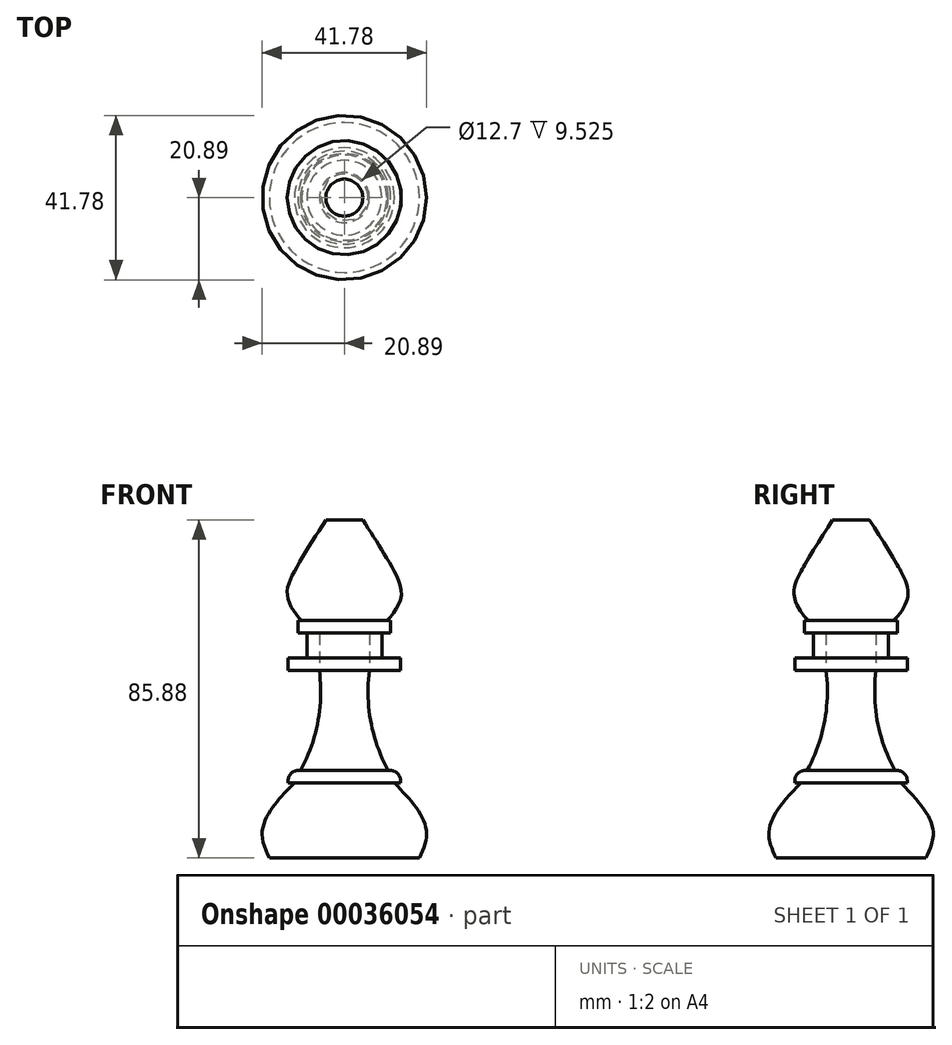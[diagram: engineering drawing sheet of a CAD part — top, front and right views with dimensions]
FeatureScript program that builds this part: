
annotation { "Feature Type Name" : "Feature", "Feature Type Description" : "" }
export const myFeature = defineFeature(function(context is Context, id is Id, definition is map)
    precondition{}
    {
        {
            var Q0;
            Q0=qCreatedBy(makeId("Top.planeOp"),FACE);
            var sketch = newSketch(context, id + "F0", { "sketchPlane" : qUnion([Q0])});
            skCircle(sketch, "E0", {"center": v(0, 0) * mm, "radius": 19.05 * mm});
            skSolve(sketch);
        }
        {
            var Q0;
            Q0=qCreatedBy(makeId("Top.planeOp"),FACE);
            cPlane(context, id + "F1", {"entities" : qUnion([Q0]), "cplaneType" : CPlaneType.OFFSET, "offset" : 19.05 * mm, "width" : 152.4 * mm, "height" : 152.4 * mm});
        }
        {
            var Q0;
            Q0=qCreatedBy(id+"F1.planeOp",FACE);
            var sketch = newSketch(context, id + "F2", { "sketchPlane" : qUnion([Q0])});
            skCircle(sketch, "E1", {"center": v(0, 0) * mm, "radius": 12.7 * mm});
            skSolve(sketch);
        }
        {
            var Q0;
            Q0=qCreatedBy(makeId("Top.planeOp"),FACE);
            cPlane(context, id + "F3", {"entities" : qUnion([Q0]), "cplaneType" : CPlaneType.OFFSET, "offset" : 5.08 * mm, "width" : 152.4 * mm, "height" : 152.4 * mm});
        }
        {
            var Q0;
            Q0=qCreatedBy(id+"F3.planeOp",FACE);
            var sketch = newSketch(context, id + "F4", { "sketchPlane" : qUnion([Q0])});
            skCircle(sketch, "E2", {"center": v(0, 0) * mm, "radius": 20.82 * mm});
            skSolve(sketch);
        }
        {
            var Q0;
            Q0=makeQuery(id+"F2.imprint","IMPRINT",FACE,{"disambiguationData":[TD([[makeQuery(id+"F2.imprint","IMPRINT",EDGE,{"derivedFrom":sQuery(id+"F2.wireOp",EDGE,"E1")}),1.0]])]});
            var Q1;
            Q1=makeQuery(id+"F4.imprint","IMPRINT",FACE,{"disambiguationData":[TD([[makeQuery(id+"F4.imprint","IMPRINT",EDGE,{"derivedFrom":sQuery(id+"F4.wireOp",EDGE,"E2")}),1.0]])]});
            var Q2;
            Q2=makeQuery(id+"F0.imprint","IMPRINT",FACE,{"disambiguationData":[TD([[makeQuery(id+"F0.imprint","IMPRINT",EDGE,{"derivedFrom":sQuery(id+"F0.wireOp",EDGE,"E0")}),1.0]])]});
            loft(context, id + "F5", {"sheetProfilesArray" : [{ "sheetProfileEntities" : qUnion([Q0]) }, { "sheetProfileEntities" : qUnion([Q1]) }, { "sheetProfileEntities" : qUnion([Q2]) }]});
        }
        {
            var Q0;
            Q0=qCreatedBy(id+"F1.planeOp",FACE);
            var sketch = newSketch(context, id + "F6", { "sketchPlane" : qUnion([Q0])});
            skCircle(sketch, "E3", {"center": v(0, 0) * mm, "radius": 14.29 * mm});
            skSolve(sketch);
        }
        {
            var Q0;
            Q0=makeQuery(id+"F6.imprint","IMPRINT",FACE,{"disambiguationData":[TD([[makeQuery(id+"F6.imprint","IMPRINT",EDGE,{"derivedFrom":sQuery(id+"F6.wireOp",EDGE,"E3")}),1.0]])]});
            var Q1;
            Q1=sQuery(id+"F6.wireOp",EDGE,"E3");
            extrude(context, id + "F7", {"entities" : qUnion([Q0]), "operationType" : NewBodyOperationType.ADD, "surfaceEntities" : qUnion([Q1]), "depth" : 3.17 * mm});
        }
        {
            var Q0;
            Q0=makeQuery(id+"F7.opExtrude","CAP_EDGE",EDGE,{"disambiguationData":[OSD([sQuery(id+"F6.wireOp",EDGE,"E3")])],"isStart":false});
            fillet(context, id + "F8", {"entities" : qUnion([Q0]), "radius" : 2.54 * mm, "tangentPropagation" : true, "allowEdgeOverflow" : false});
        }
        {
            var Q0;
            Q0=makeQuery(id+"F7.opExtrude","CAP_FACE",FACE,{"disambiguationData":[OSD([sQuery(id+"F6.wireOp",EDGE,"E3")])],"isStart":false});
            cPlane(context, id + "F9", {"entities" : qUnion([Q0]), "cplaneType" : CPlaneType.OFFSET, "offset" : 25.4 * mm, "width" : 152.4 * mm, "height" : 152.4 * mm});
        }
        {
            var Q0;
            Q0=qCreatedBy(id+"F9.planeOp",FACE);
            var sketch = newSketch(context, id + "F10", { "sketchPlane" : qUnion([Q0])});
            skCircle(sketch, "E4", {"center": v(0, 0) * mm, "radius": 6.35 * mm});
            skSolve(sketch);
        }
        {
            var Q0;
            Q0=qCreatedBy(makeId("Front.planeOp"),FACE);
            var sketch = newSketch(context, id + "F11", { "sketchPlane" : qUnion([Q0])});
            skLineSegment(sketch, "E5", {"start": v(0, 47.62) * mm, "end": v(0, 22.22) * mm});
            skLineSegment(sketch, "E6", {"start": v(0, 47.62) * mm, "end": v(6.35, 47.62) * mm});
            skArc(sketch, "E7", {"start": v(6.35, 47.62) * mm, "mid": v(6.74, 34.54) * mm, "end": v(11.16, 22.23) * mm});
            skLineSegment(sketch, "E8", {"start": v(11.16, 22.23) * mm, "end": v(0, 22.22) * mm});
            skSolve(sketch);
        }
        {
            var Q0;
            Q0=makeQuery(id+"F11.imprint","IMPRINT",FACE,{"disambiguationData":[TD([[makeQuery(id+"F11.imprint","IMPRINT",EDGE,{"derivedFrom":sQuery(id+"F11.wireOp",EDGE,"E5")}),1.0]])]});
            var Q1;
            Q1=sQuery(id+"F11.wireOp",EDGE,"E5");
            revolve(context, id + "F12", {"operationType" : NewBodyOperationType.ADD, "entities" : qUnion([Q0]), "axis" : qUnion([Q1]), "revolveType" : RevolveType.FULL});
        }
        {
            var Q0;
            Q0=makeQuery(id+"F10.imprint","IMPRINT",FACE,{"disambiguationData":[TD([[makeQuery(id+"F10.imprint","IMPRINT",EDGE,{"derivedFrom":sQuery(id+"F10.wireOp",EDGE,"E4")}),1.0]])]});
            var sketch = newSketch(context, id + "F13", { "sketchPlane" : qUnion([Q0])});
            skCircle(sketch, "E9", {"center": v(0, 0) * mm, "radius": 14.29 * mm});
            skSolve(sketch);
        }
        {
            var Q0;
            Q0=makeQuery(id+"F13.imprint","IMPRINT",FACE,{"disambiguationData":[TD([[makeQuery(id+"F13.imprint","IMPRINT",EDGE,{"derivedFrom":sQuery(id+"F13.wireOp",EDGE,"E9")}),1.0]])]});
            var Q1;
            Q1=sQuery(id+"F13.wireOp",EDGE,"E9");
            extrude(context, id + "F14", {"entities" : qUnion([Q0]), "surfaceEntities" : qUnion([Q1]), "depth" : 3.17 * mm});
        }
        {
            var Q0;
            Q0=makeQuery(id+"F14.opExtrude","CAP_FACE",FACE,{"disambiguationData":[OSD([sQuery(id+"F10.wireOp",EDGE,"E4"),sQuery(id+"F13.wireOp",EDGE,"E9")])],"isStart":false});
            var sketch = newSketch(context, id + "F15", { "sketchPlane" : qUnion([Q0])});
            skCircle(sketch, "E10", {"center": v(0, 0) * mm, "radius": 9.53 * mm});
            skSolve(sketch);
        }
        {
            var Q0;
            Q0=makeQuery(id+"F15.imprint","IMPRINT",FACE,{"disambiguationData":[TD([[makeQuery(id+"F15.imprint","IMPRINT",EDGE,{"derivedFrom":sQuery(id+"F15.wireOp",EDGE,"E10")}),1.0]])]});
            var Q1;
            Q1=sQuery(id+"F15.wireOp",EDGE,"E10");
            extrude(context, id + "F16", {"entities" : qUnion([Q0]), "operationType" : NewBodyOperationType.ADD, "surfaceEntities" : qUnion([Q1]), "depth" : 6.35 * mm});
        }
        {
            var Q0;
            Q0=makeQuery(id+"F16.opExtrude","CAP_FACE",FACE,{"disambiguationData":[OSD([sQuery(id+"F10.wireOp",EDGE,"E4"),sQuery(id+"F15.wireOp",EDGE,"E10")])],"isStart":false});
            var sketch = newSketch(context, id + "F17", { "sketchPlane" : qUnion([Q0])});
            skCircle(sketch, "E11", {"center": v(0, 0) * mm, "radius": 11.8 * mm});
            skSolve(sketch);
        }
        {
            var Q0;
            Q0=makeQuery(id+"F17.imprint","IMPRINT",FACE,{"disambiguationData":[TD([[makeQuery(id+"F17.imprint","IMPRINT",EDGE,{"derivedFrom":sQuery(id+"F17.wireOp",EDGE,"E11")}),1.0]])]});
            var Q1;
            Q1=makeQuery(id+"F17.imprint","IMPRINT",FACE,{"disambiguationData":[TD([[makeQuery(id+"F17.imprint","IMPRINT",EDGE,{"derivedFrom":makeQuery(id+"F16.opExtrude","CAP_EDGE",EDGE,{"disambiguationData":[OSD([sQuery(id+"F15.wireOp",EDGE,"E10")])],"isStart":false})}),1.0]])]});
            var Q2;
            Q2=makeQuery(id+"F17.imprint","IMPRINT",FACE,{"disambiguationData":[TD([[makeQuery(id+"F17.imprint","IMPRINT",EDGE,{"derivedFrom":makeQuery(id+"F16.opExtrude","CAP_EDGE",EDGE,{"disambiguationData":[OSD([sQuery(id+"F10.wireOp",EDGE,"E4")])],"isStart":false})}),1.0]])]});
            var Q3;
            Q3=sQuery(id+"F17.wireOp",EDGE,"E11");
            extrude(context, id + "F18", {"entities" : qUnion([Q0, Q1, Q2]), "operationType" : NewBodyOperationType.ADD, "surfaceEntities" : qUnion([Q3]), "depth" : 3.17 * mm});
        }
        {
            var Q0;
            Q0=qCreatedBy(makeId("Front.planeOp"),FACE);
            var sketch = newSketch(context, id + "F19", { "sketchPlane" : qUnion([Q0])});
            skLineSegment(sketch, "E12", {"start": v(0, 60.32) * mm, "end": v(0, 85.88) * mm});
            skLineSegment(sketch, "E13", {"start": v(0, 85.88) * mm, "end": v(4.7, 85.88) * mm});
            skFitSpline(sketch, "E14", {"points": [v(4.7, 85.88) * mm, v(12.48, 73.24) * mm, v(14.43, 66.5) * mm, v(10.82, 60.32) * mm], "startDerivative": vector(20.21, -31.24) * mm, "endDerivative": vector(-17.45, -17.5) * mm});
            skLineSegment(sketch, "E15", {"start": v(0, 60.32) * mm, "end": v(10.82, 60.32) * mm});
            skSolve(sketch);
        }
        {
            var Q0;
            Q0=makeQuery(id+"F19.imprint","IMPRINT",FACE,{"disambiguationData":[TD([[makeQuery(id+"F19.imprint","IMPRINT",EDGE,{"derivedFrom":sQuery(id+"F19.wireOp",EDGE,"E12")}),-1.0]])]});
            var Q1;
            Q1=sQuery(id+"F19.wireOp",EDGE,"E12");
            revolve(context, id + "F20", {"entities" : qUnion([Q0]), "axis" : qUnion([Q1]), "revolveType" : RevolveType.FULL});
        }
    });
